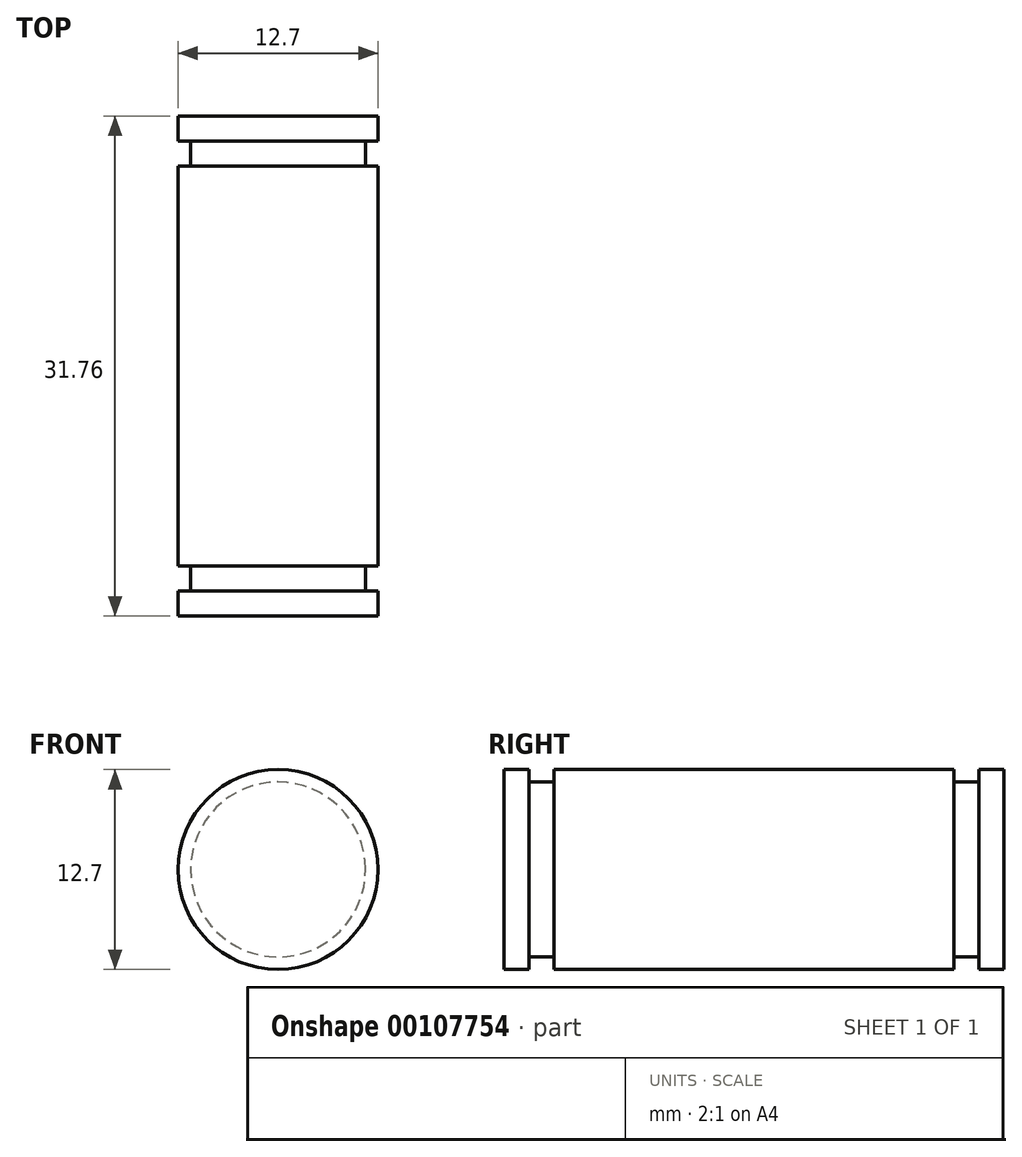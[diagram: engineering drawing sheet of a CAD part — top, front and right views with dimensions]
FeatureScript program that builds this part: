
annotation { "Feature Type Name" : "Feature", "Feature Type Description" : "" }
export const myFeature = defineFeature(function(context is Context, id is Id, definition is map)
    precondition{}
    {
        {
            var Q0;
            Q0=qCreatedBy(makeId("Front.planeOp"),FACE);
            var sketch = newSketch(context, id + "F0", { "sketchPlane" : qUnion([Q0])});
            skCircle(sketch, "E0", {"center": v(0, 0) * mm, "radius": 6.35 * mm});
            skSolve(sketch);
        }
        {
            var Q0;
            Q0=makeQuery(id+"F0.imprint","IMPRINT",FACE,{"disambiguationData":[TD([[makeQuery(id+"F0.imprint","IMPRINT",EDGE,{"derivedFrom":sQuery(id+"F0.wireOp",EDGE,"E0")}),1.0]])]});
            var Q1;
            Q1 = qSketchRegion(id + "F0", true);
            extrude(context, id + "F1", {"entities" : qUnion([Q0, Q1]), "depth" : 25.4 * mm});
        }
        {
            var Q0;
            Q0=makeQuery(id+"F1.opExtrude","CAP_FACE",FACE,{"disambiguationData":[OSD([sQuery(id+"F0.wireOp",EDGE,"E0")])],"isStart":false});
            var sketch = newSketch(context, id + "F2", { "sketchPlane" : qUnion([Q0])});
            skCircle(sketch, "E1", {"center": v(0, 0) * mm, "radius": 5.56 * mm});
            skSolve(sketch);
        }
        {
            var Q0;
            Q0 = qSketchRegion(id + "F2", true);
            extrude(context, id + "F3", {"entities" : qUnion([Q0]), "operationType" : NewBodyOperationType.ADD, "depth" : 1.59 * mm});
        }
        {
            var Q0;
            Q0=makeQuery(id+"F3.opExtrude","CAP_FACE",FACE,{"disambiguationData":[OSD([sQuery(id+"F2.wireOp",EDGE,"E1")])],"isStart":false});
            var sketch = newSketch(context, id + "F4", { "sketchPlane" : qUnion([Q0])});
            skCircle(sketch, "E2", {"center": v(0, 0) * mm, "radius": 6.35 * mm});
            skSolve(sketch);
        }
        {
            var Q0;
            Q0 = qSketchRegion(id + "F4", true);
            extrude(context, id + "F5", {"entities" : qUnion([Q0]), "operationType" : NewBodyOperationType.ADD, "depth" : 1.59 * mm});
        }
        {
            var Q0;
            Q0=makeQuery(id+"F1.opExtrude","CAP_FACE",FACE,{"disambiguationData":[OSD([sQuery(id+"F0.wireOp",EDGE,"E0")])],"isStart":true});
            var sketch = newSketch(context, id + "F6", { "sketchPlane" : qUnion([Q0])});
            skCircle(sketch, "E3", {"center": v(0, 0) * mm, "radius": 5.56 * mm});
            skSolve(sketch);
        }
        {
            var Q0;
            Q0 = qSketchRegion(id + "F6", true);
            extrude(context, id + "F7", {"entities" : qUnion([Q0]), "operationType" : NewBodyOperationType.ADD, "depth" : 1.59 * mm});
        }
        {
            var Q0;
            Q0=makeQuery(id+"F7.opExtrude","CAP_FACE",FACE,{"disambiguationData":[OSD([sQuery(id+"F6.wireOp",EDGE,"E3")])],"isStart":false});
            var sketch = newSketch(context, id + "F8", { "sketchPlane" : qUnion([Q0])});
            skCircle(sketch, "E4", {"center": v(0, 0) * mm, "radius": 6.35 * mm});
            skSolve(sketch);
        }
        {
            var Q0;
            Q0 = qSketchRegion(id + "F8", true);
            extrude(context, id + "F9", {"entities" : qUnion([Q0]), "operationType" : NewBodyOperationType.ADD, "depth" : 1.59 * mm});
        }
    });
